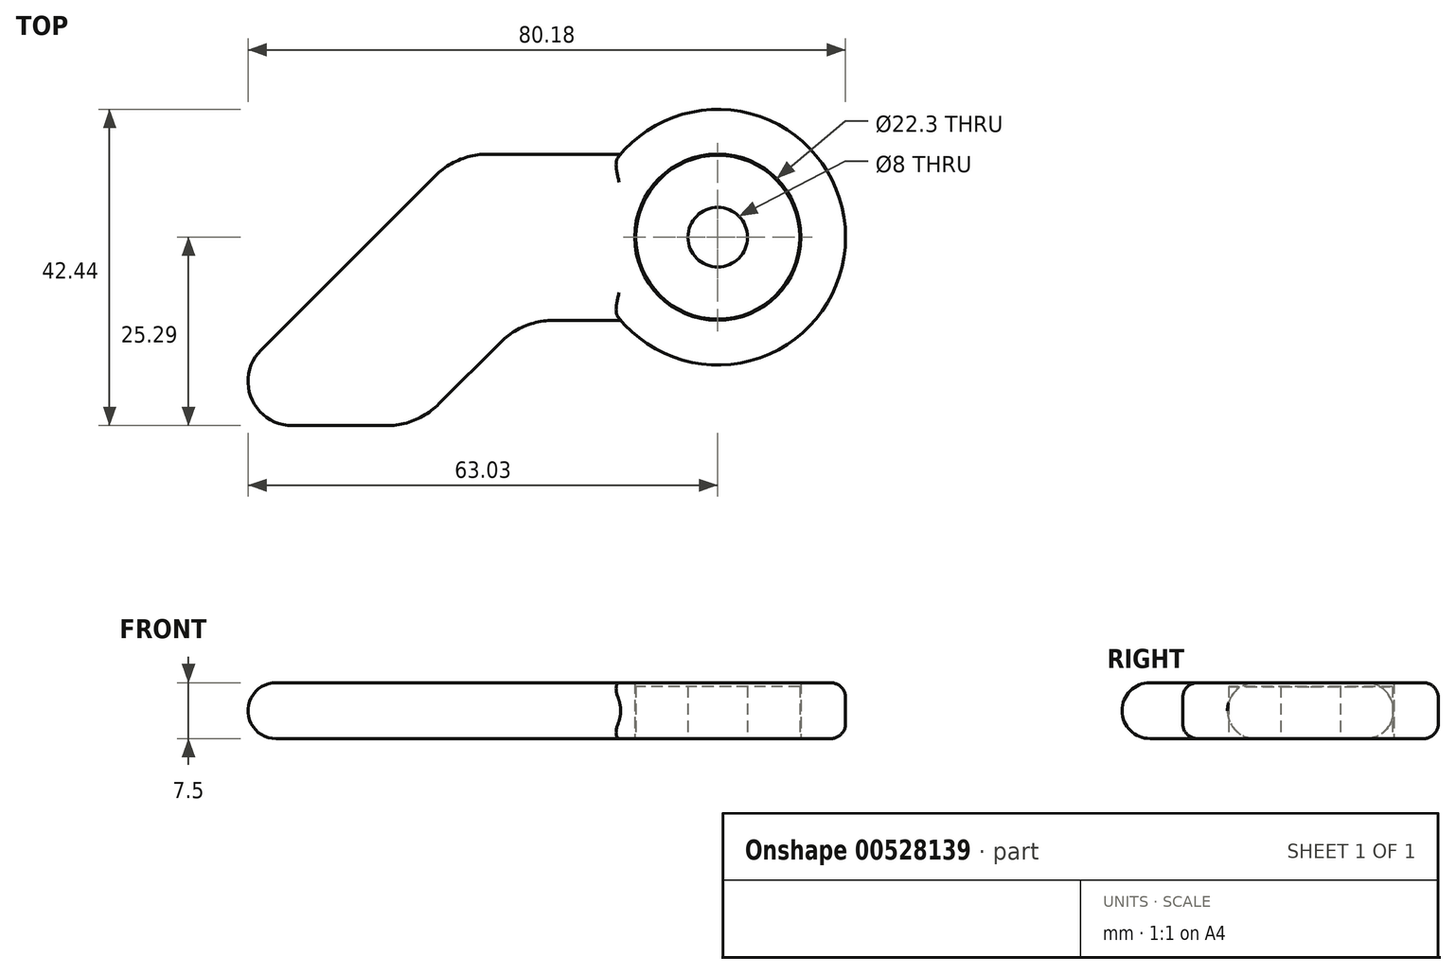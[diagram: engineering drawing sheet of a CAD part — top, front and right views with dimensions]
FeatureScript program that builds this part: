
annotation { "Feature Type Name" : "Feature", "Feature Type Description" : "" }
export const myFeature = defineFeature(function(context is Context, id is Id, definition is map)
    precondition{}
    {
        {
            var Q0;
            Q0=qCreatedBy(makeId("Top.planeOp"),FACE);
            var sketch = newSketch(context, id + "F0", { "sketchPlane" : qUnion([Q0])});
            skCircle(sketch, "E0", {"center": v(0, 0) * mm, "radius": 11 * mm});
            skCircle(sketch, "E1", {"center": v(0, 0) * mm, "radius": 4 * mm});
            skSolve(sketch);
        }
        {
            var Q0;
            Q0=makeQuery(id+"F0.imprint","IMPRINT",FACE,{"disambiguationData":[TD([[makeQuery(id+"F0.imprint","IMPRINT",EDGE,{"derivedFrom":sQuery(id+"F0.wireOp",EDGE,"E0")}),1.0]])]});
            extrude(context, id + "F1", {"entities" : qUnion([Q0]), "depth" : 7 * mm, "offsetDistance" : 25 * mm});
        }
        {
            var Q0;
            Q0=qCreatedBy(makeId("Top.planeOp"),FACE);
            var sketch = newSketch(context, id + "F2", { "sketchPlane" : qUnion([Q0])});
            skCircle(sketch, "E2.0", {"center": v(0, 0) * mm, "radius": 11.15 * mm});
            skLineSegment(sketch, "E3.bottom", {"start": v(-13.03, 11.15) * mm, "end": v(-30.86, 11.15) * mm});
            skLineSegment(sketch, "E3.top", {"start": v(-13.03, -11.15) * mm, "end": v(-22.05, -11.15) * mm});
            skPoint(sketch, "E3.left.start.orphan", {"position": v(45.03, 11.15) * mm});
            skPoint(sketch, "E4.orphan", {"position": v(35, -11.15) * mm});
            skLineSegment(sketch, "E5", {"start": v(-37.93, 8.22) * mm, "end": v(-61.3, -15.14) * mm});
            skLineSegment(sketch, "E6", {"start": v(-57.09, -25.3) * mm, "end": v(-44.47, -25.3) * mm});
            skLineSegment(sketch, "E7", {"start": v(-37.4, -22.36) * mm, "end": v(-29.12, -14.08) * mm});
            skPoint(sketch, "E8.orphan", {"position": v(-45.03, -11.15) * mm});
            skPoint(sketch, "E9.visualSharp", {"position": v(-35, 11.15) * mm});
            skArc(sketch, "E9.filletArc", {"start": v(-30.86, 11.15) * mm, "mid": v(-34.68, 10.39) * mm, "end": v(-37.93, 8.22) * mm});
            skPoint(sketch, "E10.visualSharp", {"position": v(-26.19, -11.15) * mm});
            skArc(sketch, "E10.filletArc", {"start": v(-22.05, -11.15) * mm, "mid": v(-25.87, -11.91) * mm, "end": v(-29.12, -14.08) * mm});
            skPoint(sketch, "E11.visualSharp", {"position": v(-40.33, -25.3) * mm});
            skArc(sketch, "E11.filletArc", {"start": v(-44.47, -25.3) * mm, "mid": v(-40.64, -24.53) * mm, "end": v(-37.4, -22.36) * mm});
            skPoint(sketch, "E12.visualSharp", {"position": v(-71.44, -25.3) * mm});
            skArc(sketch, "E12.filletArc", {"start": v(-61.3, -15.14) * mm, "mid": v(-62.58, -21.62) * mm, "end": v(-57.09, -25.3) * mm});
            skArc(sketch, "E13.0", {"start": v(-13.03, -11.15) * mm, "mid": v(17.15, 0) * mm, "end": v(-13.03, 11.15) * mm});
            skPoint(sketch, "E14.orphan", {"position": v(0, 11.15) * mm});
            skCircle(sketch, "E15.0", {"center": v(0, 0) * mm, "radius": 17.15 * mm});
            skSolve(sketch);
        }
        {
            var Q0;
            Q0=makeQuery(id+"F2.imprint","IMPRINT",FACE,{"disambiguationData":[TD([[makeQuery(id+"F2.imprint","IMPRINT",EDGE,{"derivedFrom":sQuery(id+"F2.wireOp",EDGE,"E2.0")}),-1.0]])]});
            extrude(context, id + "F3", {"entities" : qUnion([Q0]), "depth" : 7.5 * mm, "offsetDistance" : 25 * mm});
        }
        {
            var Q0;
            {var subQ1=sQuery(id+"F2.wireOp",EDGE,"E3.bottom");Q0=makeQuery(id+"F2.imprint","IMPRINT",FACE,{"disambiguationData":[TD([[makeQuery(id+"F2.imprint","IMPRINT",EDGE,{"derivedFrom":subQ1}),1.0]])]});}
            extrude(context, id + "F4", {"entities" : qUnion([Q0]), "operationType" : NewBodyOperationType.ADD, "depth" : 7.5 * mm, "offsetDistance" : 25 * mm});
        }
        {
            var Q0;
            Q0=makeQuery(id+"F4.opExtrude","CAP_EDGE",EDGE,{"disambiguationData":[OSD([sQuery(id+"F2.wireOp",EDGE,"E3.bottom")])],"isStart":false});
            var Q1;
            Q1=makeQuery(id+"F4.opExtrude","CAP_EDGE",EDGE,{"disambiguationData":[OSD([sQuery(id+"F2.wireOp",EDGE,"E3.top")])],"isStart":false});
            var Q2;
            Q2=makeQuery(id+"F4.opExtrude","CAP_EDGE",EDGE,{"disambiguationData":[OSD([sQuery(id+"F2.wireOp",EDGE,"E5")])],"isStart":true});
            var Q3;
            Q3=makeQuery(id+"F4.opExtrude","CAP_EDGE",EDGE,{"disambiguationData":[OSD([sQuery(id+"F2.wireOp",EDGE,"E10.filletArc")])],"isStart":true});
            var Q4;
            Q4=makeQuery(id+"F4.opExtrude","CAP_EDGE",EDGE,{"disambiguationData":[OSD([sQuery(id+"F2.wireOp",EDGE,"E3.top")])],"isStart":true});
            fillet(context, id + "F5", {"entities" : qUnion([Q0, Q1, Q2, Q3, Q4]), "radius" : 3.75 * mm, "tangentPropagation" : true, "allowEdgeOverflow" : false});
        }
        {
            var Q0;
            {var subQ1=sQuery(id+"F2.wireOp",EDGE,"E15.0");var subQ9=sQuery(id+"F2.wireOp",EDGE,"E3.bottom");Q0=makeQuery(id+"FXRLM3DIeddr7JO_2.1.F4.boolean.opBoolean","SPLIT",EDGE,{"disambiguationData":[TD([makeQuery(id+"FXRLM3DIeddr7JO_2.1.F4.opExtrude","SWEPT_FACE",FACE,{"disambiguationData":[OSD([subQ9])]})])],"derivedFrom":makeQuery(id+"F3.opExtrude","CAP_EDGE",EDGE,{"disambiguationData":[OSD([subQ1])],"isStart":false})});}
            var Q1;
            {var subQ1=sQuery(id+"F2.wireOp",EDGE,"E15.0");var subQ9=sQuery(id+"F2.wireOp",EDGE,"E3.top");Q1=makeQuery(id+"FXRLM3DIeddr7JO_2.1.F4.boolean.opBoolean","SPLIT",EDGE,{"disambiguationData":[TD([makeQuery(id+"FXRLM3DIeddr7JO_2.1.F4.opExtrude","SWEPT_FACE",FACE,{"disambiguationData":[OSD([subQ9])]})])],"derivedFrom":makeQuery(id+"F3.opExtrude","CAP_EDGE",EDGE,{"disambiguationData":[OSD([subQ1])],"isStart":false})});}
            var Q2;
            {var subQ1=sQuery(id+"F2.wireOp",EDGE,"E15.0");var subQ9=sQuery(id+"F2.wireOp",EDGE,"E3.bottom");Q2=makeQuery(id+"FXRLM3DIeddr7JO_2.1.F4.boolean.opBoolean","SPLIT",EDGE,{"disambiguationData":[TD([makeQuery(id+"FXRLM3DIeddr7JO_2.1.F4.opExtrude","SWEPT_FACE",FACE,{"disambiguationData":[OSD([subQ9])]})])],"derivedFrom":makeQuery(id+"F3.opExtrude","CAP_EDGE",EDGE,{"disambiguationData":[OSD([subQ1])],"isStart":true})});}
            var Q3;
            {var subQ0=sQuery(id+"F2.wireOp",EDGE,"E15.0");var subQ8=sQuery(id+"F2.wireOp",EDGE,"E3.top");Q3=makeQuery(id+"FXRLM3DIeddr7JO_2.1.F4.boolean.opBoolean","SPLIT",EDGE,{"disambiguationData":[TD([makeQuery(id+"FXRLM3DIeddr7JO_2.1.F4.opExtrude","SWEPT_FACE",FACE,{"disambiguationData":[OSD([subQ8])]})])],"derivedFrom":makeQuery(id+"F3.opExtrude","CAP_EDGE",EDGE,{"disambiguationData":[OSD([subQ0])],"isStart":true})});}
            var Q4;
            Q4=makeQuery(id+"F4.opExtrude","SWEPT_EDGE",EDGE,{"disambiguationData":[OSD([sQuery(id+"F2.wireOp",EDGE,"E3.top"),sQuery(id+"F2.wireOp",EDGE,"E15.0")])]});
            var Q5;
            Q5=makeQuery(id+"FXRLM3DIeddr7JO_2.1.F4.opExtrude","SWEPT_EDGE",EDGE,{"disambiguationData":[OSD([sQuery(id+"F2.wireOp",EDGE,"E3.bottom"),sQuery(id+"F2.wireOp",EDGE,"E15.0")])]});
            var Q6;
            Q6=makeQuery(id+"FXRLM3DIeddr7JO_2.1.F4.opExtrude","SWEPT_EDGE",EDGE,{"disambiguationData":[OSD([sQuery(id+"F2.wireOp",EDGE,"E3.top"),sQuery(id+"F2.wireOp",EDGE,"E15.0")])]});
            var Q7;
            Q7=makeQuery(id+"F4.opExtrude","SWEPT_EDGE",EDGE,{"disambiguationData":[OSD([sQuery(id+"F2.wireOp",EDGE,"E3.bottom"),sQuery(id+"F2.wireOp",EDGE,"E15.0")])]});
            fillet(context, id + "F6", {"entities" : qUnion([Q0, Q1, Q2, Q3, Q4, Q5, Q6, Q7]), "radius" : 2 * mm, "tangentPropagation" : true, "allowEdgeOverflow" : false});
        }
    });
